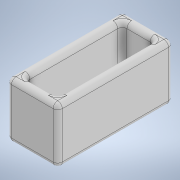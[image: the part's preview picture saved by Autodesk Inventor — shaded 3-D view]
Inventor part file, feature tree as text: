
AUTODESK INVENTOR PART (.ipt)
format: ipt  version: 2020 (Build 240168000, 168)  size: 182,272 bytes
history: native  units: in
note: dims shown in document units (in); Inventor stores cm internally (conversion verified against a paired STEP export)
features: extrude x2, fillet x2, sketch x2
ambient origin geometry x8: Origin, YZ Plane, XZ Plane, XY Plane, X Axis, Y Axis, Z Axis, Center Point
bodies: Solid1 (feature_tree)
feature tree (6):
  extrude  "Extrusion1"  Depth=0.8268in
  extrude  "Extrusion2"  Depth=0.0787in
  fillet  "Fillet1"  Radius=0.0787in
  fillet  "Fillet2"  Radius=0.0787in
  sketch  "Sketch1"  dims[d0=0.2756in d1=0.8268in]
  sketch  "Sketch2"  dims[d2=0.0787in d3=0.0787in d4=0.0787in d5=0.0787in d6=0.0787in d7=0.0in d8=0.0787in d9=0.0787in d10=0.0787in d11=0.0787in d12=0.3937in d13=0.0in d14=0.0394in d15=0.0394in]
